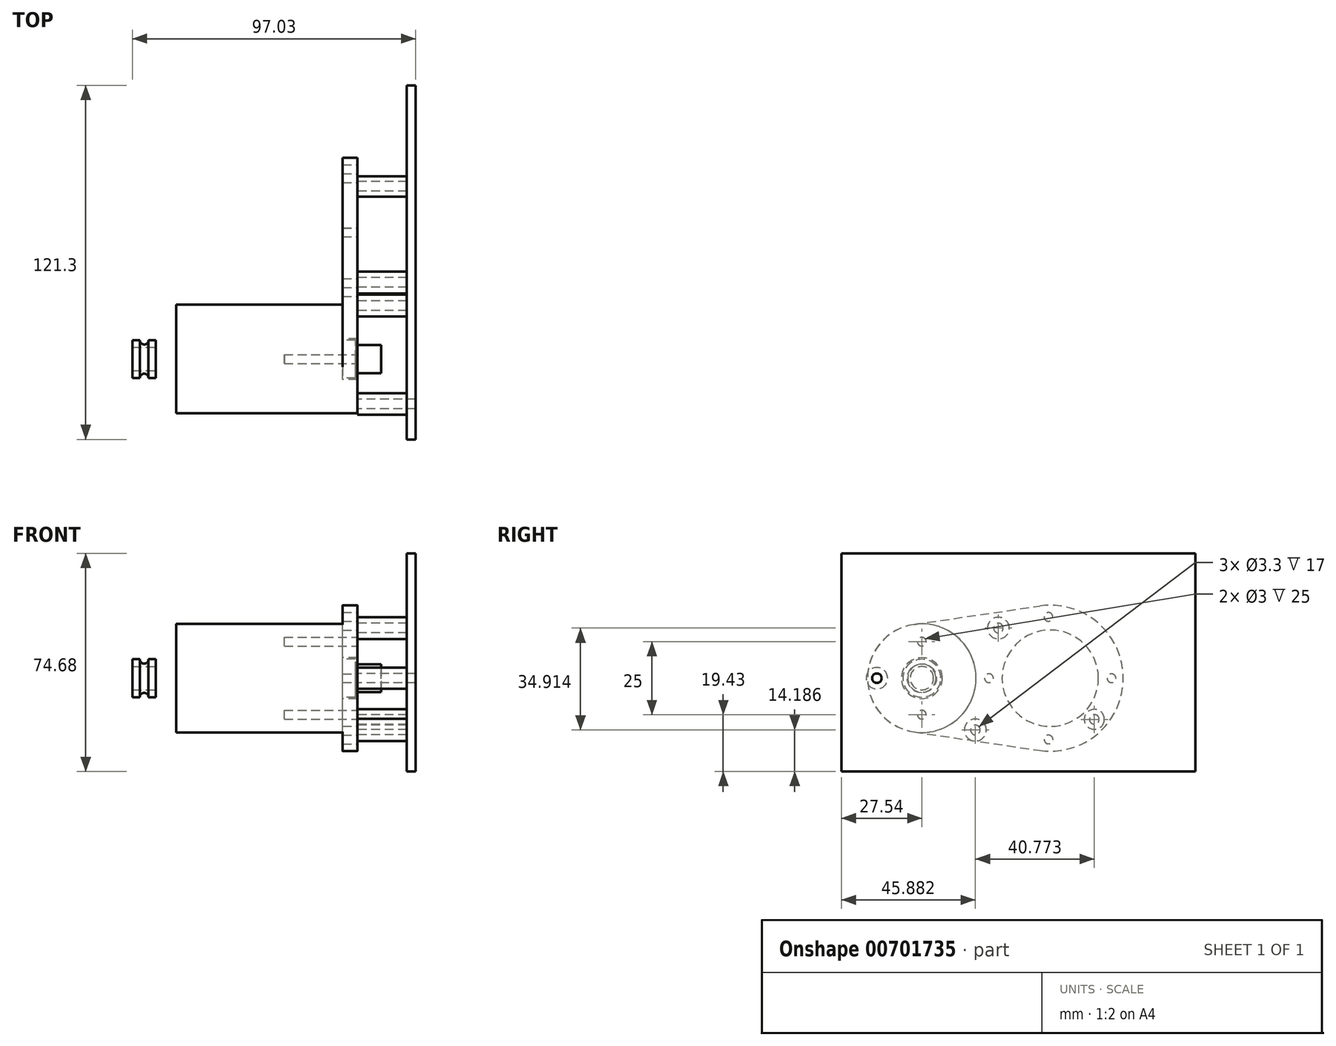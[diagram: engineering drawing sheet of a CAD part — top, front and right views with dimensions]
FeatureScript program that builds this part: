
annotation { "Feature Type Name" : "Feature", "Feature Type Description" : "" }
export const myFeature = defineFeature(function(context is Context, id is Id, definition is map)
    precondition{}
    {
        {
            var Q0;
            Q0=qCreatedBy(makeId("Right.planeOp"),FACE);
            var sketch = newSketch(context, id + "F0", { "sketchPlane" : qUnion([Q0])});
            skCircle(sketch, "E0", {"center": v(0, 0) * mm, "radius": 18.6 * mm});
            skSolve(sketch);
        }
        {
            var Q0;
            Q0=makeQuery(id+"F0.imprint","IMPRINT",FACE,{"disambiguationData":[TD([[makeQuery(id+"F0.imprint","IMPRINT",EDGE,{"derivedFrom":sQuery(id+"F0.wireOp",EDGE,"E0")}),1.0]])]});
            extrude(context, id + "F1", {"entities" : qUnion([Q0]), "depth" : 57 * mm, "offsetDistance" : 25 * mm});
        }
        {
            var Q0;
            Q0=makeQuery(id+"F1.opExtrude","CAP_FACE",FACE,{"disambiguationData":[OSD([sQuery(id+"F0.wireOp",EDGE,"E0")])],"isStart":false});
            var sketch = newSketch(context, id + "F2", { "sketchPlane" : qUnion([Q0])});
            skCircle(sketch, "E1", {"center": v(0, 0) * mm, "radius": 6.5 * mm});
            skSolve(sketch);
        }
        {
            var Q0;
            Q0=makeQuery(id+"F2.imprint","IMPRINT",FACE,{"disambiguationData":[TD([[makeQuery(id+"F2.imprint","IMPRINT",EDGE,{"derivedFrom":sQuery(id+"F2.wireOp",EDGE,"E1")}),1.0]])]});
            extrude(context, id + "F3", {"entities" : qUnion([Q0]), "operationType" : NewBodyOperationType.ADD, "depth" : 4.4 * mm, "offsetDistance" : 25 * mm});
        }
        {
            var Q0;
            Q0=makeQuery(id+"F3.opExtrude","CAP_FACE",FACE,{"disambiguationData":[OSD([sQuery(id+"F2.wireOp",EDGE,"E1")])],"isStart":false});
            var sketch = newSketch(context, id + "F4", { "sketchPlane" : qUnion([Q0])});
            skCircle(sketch, "E2", {"center": v(0, 0) * mm, "radius": 4.8 * mm});
            skSolve(sketch);
        }
        {
            var Q0;
            Q0=makeQuery(id+"F4.imprint","IMPRINT",FACE,{"disambiguationData":[TD([[makeQuery(id+"F4.imprint","IMPRINT",EDGE,{"derivedFrom":sQuery(id+"F4.wireOp",EDGE,"E2")}),1.0]])]});
            extrude(context, id + "F5", {"entities" : qUnion([Q0]), "operationType" : NewBodyOperationType.ADD, "depth" : 8.8 * mm, "offsetDistance" : 25 * mm});
        }
        {
            var Q0;
            Q0=makeQuery(id+"F1.opExtrude","CAP_FACE",FACE,{"disambiguationData":[OSD([sQuery(id+"F0.wireOp",EDGE,"E0")])],"isStart":false});
            var sketch = newSketch(context, id + "F6", { "sketchPlane" : qUnion([Q0])});
            skCircle(sketch, "E3", {"center": v(0, 0) * mm, "radius": 7 * mm});
            skCircle(sketch, "E4", {"center": v(0, 0) * mm, "radius": 20 * mm});
            skSolve(sketch);
        }
        {
            var Q0;
            Q0=makeQuery(id+"F6.imprint","IMPRINT",FACE,{"disambiguationData":[TD([[makeQuery(id+"F6.imprint","IMPRINT",EDGE,{"derivedFrom":sQuery(id+"F6.wireOp",EDGE,"E3")}),-1.0]])]});
            extrude(context, id + "F7", {"entities" : qUnion([Q0]), "depth" : 5 * mm, "offsetDistance" : 25 * mm});
        }
        {
            var Q0;
            Q0=makeQuery(id+"F7.opExtrude","CAP_FACE",FACE,{"disambiguationData":[OSD([sQuery(id+"F0.wireOp",EDGE,"E0"),sQuery(id+"F6.wireOp",EDGE,"E3")])],"isStart":false});
            var sketch = newSketch(context, id + "F8", { "sketchPlane" : qUnion([Q0])});
            skCircle(sketch, "E5", {"center": v(45, 0) * mm, "radius": 25 * mm});
            skCircle(sketch, "E6", {"center": v(45, 0) * mm, "radius": 16.5 * mm});
            skSolve(sketch);
        }
        {
            var Q0;
            Q0=makeQuery(id+"F8.imprint","IMPRINT",FACE,{"disambiguationData":[TD([[makeQuery(id+"F8.imprint","IMPRINT",EDGE,{"derivedFrom":sQuery(id+"F8.wireOp",EDGE,"E5")}),1.0]])]});
            extrude(context, id + "F9", {"entities" : qUnion([Q0]), "oppositeDirection" : true, "depth" : 5 * mm, "offsetDistance" : 25 * mm});
        }
        {
            var Q0;
            Q0=makeQuery(id+"F9.opExtrude","SWEPT_BODY",BODY,{"disambiguationData":[OSD([sQuery(id+"F8.wireOp",EDGE,"E5"),sQuery(id+"F8.wireOp",EDGE,"E6")])]});
            deleteBodies(context, id + "F10", {"entities" : qUnion([Q0])});
        }
        {
            var Q0;
            Q0=makeQuery(id+"F7.opExtrude","CAP_FACE",FACE,{"disambiguationData":[OSD([sQuery(id+"F0.wireOp",EDGE,"E0"),sQuery(id+"F6.wireOp",EDGE,"E3")])],"isStart":false});
            var sketch = newSketch(context, id + "F11", { "sketchPlane" : qUnion([Q0])});
            skLineSegment(sketch, "E7", {"start": v(-2.7, 18.4) * mm, "end": v(40.36, 24.73) * mm});
            skLineSegment(sketch, "E8", {"start": v(-2.7, -18.4) * mm, "end": v(40.36, -24.73) * mm});
            skArc(sketch, "E9", {"start": v(40.36, 24.73) * mm, "mid": v(69, 0) * mm, "end": v(40.36, -24.73) * mm});
            skCircle(sketch, "E10", {"center": v(44, 0) * mm, "radius": 16.5 * mm});
            skArc(sketch, "E11", {"start": v(-2.7, 18.4) * mm, "mid": v(18.6, 0) * mm, "end": v(-2.7, -18.4) * mm});
            skSolve(sketch);
        }
        {
            var Q0;
            Q0=makeQuery(id+"F11.imprint","IMPRINT",FACE,{"disambiguationData":[TD([[makeQuery(id+"F11.imprint","IMPRINT",EDGE,{"derivedFrom":sQuery(id+"F11.wireOp",EDGE,"E7")}),-1.0]])]});
            extrude(context, id + "F12", {"entities" : qUnion([Q0]), "operationType" : NewBodyOperationType.ADD, "oppositeDirection" : true, "depth" : 5 * mm, "offsetDistance" : 25 * mm});
        }
        {
            var Q0;
            Q0=makeQuery(id+"F12.boolean.opBoolean","MERGE",FACE,{"derivedFrom":[makeQuery(id+"F7.opExtrude","CAP_FACE",FACE,{"disambiguationData":[OSD([sQuery(id+"F0.wireOp",EDGE,"E0"),sQuery(id+"F6.wireOp",EDGE,"E3")])],"isStart":false}),makeQuery(id+"F12.opExtrude","CAP_FACE",FACE,{"disambiguationData":[OSD([sQuery(id+"F11.wireOp",EDGE,"E7"),sQuery(id+"F11.wireOp",EDGE,"E8"),sQuery(id+"F11.wireOp",EDGE,"E9"),sQuery(id+"F11.wireOp",EDGE,"E10"),sQuery(id+"F11.wireOp",EDGE,"E11")])],"isStart":true})]});
            var sketch = newSketch(context, id + "F13", { "sketchPlane" : qUnion([Q0])});
            skCircle(sketch, "E12", {"center": v(0, 12.5) * mm, "radius": 1.5 * mm});
            skCircle(sketch, "E13", {"center": v(0, -12.5) * mm, "radius": 1.5 * mm});
            skSolve(sketch);
        }
        {
            var Q0;
            Q0=makeQuery(id+"F13.imprint","IMPRINT",FACE,{"disambiguationData":[TD([[makeQuery(id+"F13.imprint","IMPRINT",EDGE,{"derivedFrom":sQuery(id+"F13.wireOp",EDGE,"E12")}),1.0]])]});
            var Q1;
            Q1=makeQuery(id+"F13.imprint","IMPRINT",FACE,{"disambiguationData":[TD([[makeQuery(id+"F13.imprint","IMPRINT",EDGE,{"derivedFrom":sQuery(id+"F13.wireOp",EDGE,"E13")}),1.0]])]});
            extrude(context, id + "F14", {"entities" : qUnion([Q0, Q1]), "operationType" : NewBodyOperationType.REMOVE, "oppositeDirection" : true, "depth" : 25 * mm, "offsetDistance" : 25 * mm});
        }
        {
            var Q0;
            Q0=makeQuery(id+"F12.boolean.opBoolean","MERGE",FACE,{"derivedFrom":[makeQuery(id+"F7.opExtrude","CAP_FACE",FACE,{"disambiguationData":[OSD([sQuery(id+"F0.wireOp",EDGE,"E0"),sQuery(id+"F6.wireOp",EDGE,"E3")])],"isStart":false}),makeQuery(id+"F12.opExtrude","CAP_FACE",FACE,{"disambiguationData":[OSD([sQuery(id+"F11.wireOp",EDGE,"E7"),sQuery(id+"F11.wireOp",EDGE,"E8"),sQuery(id+"F11.wireOp",EDGE,"E9"),sQuery(id+"F11.wireOp",EDGE,"E10"),sQuery(id+"F11.wireOp",EDGE,"E11")])],"isStart":true})]});
            var sketch = newSketch(context, id + "F15", { "sketchPlane" : qUnion([Q0])});
            skCircle(sketch, "E14", {"center": v(44, 0) * mm, "radius": 21 * mm, "construction": true});
            skCircle(sketch, "E15", {"center": v(43.39, 21) * mm, "radius": 1.5 * mm});
            skCircle(sketch, "E16", {"center": v(65, 0) * mm, "radius": 1.5 * mm});
            skPoint(sketch, "E16.centerSnap0", {"position": v(69, 0) * mm});
            skCircle(sketch, "E17", {"center": v(43.43, -21) * mm, "radius": 1.5 * mm});
            skCircle(sketch, "E18", {"center": v(23, 0) * mm, "radius": 1.5 * mm});
            skSolve(sketch);
        }
        {
            var Q0;
            Q0=makeQuery(id+"F15.imprint","IMPRINT",FACE,{"disambiguationData":[TD([[makeQuery(id+"F15.imprint","IMPRINT",EDGE,{"derivedFrom":sQuery(id+"F15.wireOp",EDGE,"E18")}),1.0]])]});
            var Q1;
            Q1=makeQuery(id+"F15.imprint","IMPRINT",FACE,{"disambiguationData":[TD([[makeQuery(id+"F15.imprint","IMPRINT",EDGE,{"derivedFrom":sQuery(id+"F15.wireOp",EDGE,"E15")}),1.0]])]});
            var Q2;
            Q2=makeQuery(id+"F15.imprint","IMPRINT",FACE,{"disambiguationData":[TD([[makeQuery(id+"F15.imprint","IMPRINT",EDGE,{"derivedFrom":sQuery(id+"F15.wireOp",EDGE,"E16")}),1.0]])]});
            var Q3;
            Q3=makeQuery(id+"F15.imprint","IMPRINT",FACE,{"disambiguationData":[TD([[makeQuery(id+"F15.imprint","IMPRINT",EDGE,{"derivedFrom":sQuery(id+"F15.wireOp",EDGE,"E17")}),1.0]])]});
            extrude(context, id + "F16", {"entities" : qUnion([Q0, Q1, Q2, Q3]), "operationType" : NewBodyOperationType.REMOVE, "oppositeDirection" : true, "depth" : 25 * mm, "offsetDistance" : 25 * mm});
        }
        {
            var Q0;
            Q0=qCreatedBy(makeId("Front.planeOp"),FACE);
            var sketch = newSketch(context, id + "F17", { "sketchPlane" : qUnion([Q0])});
            skLineSegment(sketch, "E19", {"start": v(0, 0) * mm, "end": v(-20.34, 0) * mm});
            skLineSegment(sketch, "E20", {"start": v(-15.03, 4) * mm, "end": v(-15.03, 6.5) * mm});
            skLineSegment(sketch, "E21", {"start": v(-15.03, 6.5) * mm, "end": v(-12.53, 6.5) * mm});
            skLineSegment(sketch, "E22", {"start": v(-7.03, 4) * mm, "end": v(-7.03, 6.5) * mm});
            skLineSegment(sketch, "E23", {"start": v(-7.03, 6.5) * mm, "end": v(-9.53, 6.5) * mm});
            skLineSegment(sketch, "E24", {"start": v(-15.03, 4) * mm, "end": v(-7.03, 4) * mm});
            skArc(sketch, "E25", {"start": v(-12.53, 6.5) * mm, "mid": v(-11.03, 5) * mm, "end": v(-9.53, 6.5) * mm});
            skSolve(sketch);
        }
        {
            var Q0;
            Q0=makeQuery(id+"F17.imprint","IMPRINT",FACE,{"disambiguationData":[TD([[makeQuery(id+"F17.imprint","IMPRINT",EDGE,{"derivedFrom":sQuery(id+"F17.wireOp",EDGE,"E20")}),-1.0]])]});
            var Q1;
            Q1=sQuery(id+"F17.wireOp",EDGE,"E19");
            revolve(context, id + "F18", {"entities" : qUnion([Q0]), "axis" : qUnion([Q1]), "revolveType" : RevolveType.FULL});
        }
        {
            var Q0;
            Q0=makeQuery(id+"F12.boolean.opBoolean","MERGE",FACE,{"derivedFrom":[makeQuery(id+"F7.opExtrude","CAP_FACE",FACE,{"disambiguationData":[OSD([sQuery(id+"F0.wireOp",EDGE,"E0"),sQuery(id+"F6.wireOp",EDGE,"E3")])],"isStart":false}),makeQuery(id+"F12.opExtrude","CAP_FACE",FACE,{"disambiguationData":[OSD([sQuery(id+"F11.wireOp",EDGE,"E7"),sQuery(id+"F11.wireOp",EDGE,"E8"),sQuery(id+"F11.wireOp",EDGE,"E9"),sQuery(id+"F11.wireOp",EDGE,"E10"),sQuery(id+"F11.wireOp",EDGE,"E11")])],"isStart":true})]});
            var sketch = newSketch(context, id + "F19", { "sketchPlane" : qUnion([Q0])});
            skCircle(sketch, "E26", {"center": v(0, 0) * mm, "radius": 7 * mm});
            skCircle(sketch, "E27", {"center": v(44, 0) * mm, "radius": 37 * mm});
            skSolve(sketch);
        }
        {
            var Q0;
            {var subQ1=sQuery(id+"F19.wireOp",EDGE,"E26");Q0=makeQuery(id+"F19.imprint","IMPRINT",FACE,{"disambiguationData":[TD([[makeQuery(id+"F19.imprint","IMPRINT",EDGE,{"derivedFrom":subQ1}),-1.0]])]});}
            var sketch = newSketch(context, id + "F20", { "sketchPlane" : qUnion([Q0])});
            skCircle(sketch, "E28", {"center": v(-15.42, 0) * mm, "radius": 1.65 * mm});
            skCircle(sketch, "E29", {"center": v(26.23, 17.17) * mm, "radius": 1.65 * mm});
            skCircle(sketch, "E30", {"center": v(59.11, -14.1) * mm, "radius": 1.65 * mm});
            skCircle(sketch, "E31", {"center": v(18.34, -17.74) * mm, "radius": 1.65 * mm});
            skCircle(sketch, "E32", {"center": v(26.23, 17.17) * mm, "radius": 3.73 * mm});
            skCircle(sketch, "E33", {"center": v(59.11, -14.1) * mm, "radius": 3.44 * mm});
            skCircle(sketch, "E34", {"center": v(18.34, -17.74) * mm, "radius": 3.78 * mm});
            skCircle(sketch, "E35", {"center": v(-15.42, 0) * mm, "radius": 3.68 * mm});
            skSolve(sketch);
        }
        {
            var Q0;
            Q0=qSketchRegion(id+"F20",true);
            extrude(context, id + "F21", {"entities" : qUnion([Q0]), "depth" : 20 * mm, "offsetDistance" : 25 * mm});
        }
        {
            var Q0;
            Q0=makeQuery(id+"F21.opExtrude","CAP_FACE",FACE,{"disambiguationData":[OSD([sQuery(id+"F20.wireOp",EDGE,"E28"),sQuery(id+"F20.wireOp",EDGE,"E35")])],"isStart":false});
            var sketch = newSketch(context, id + "F22", { "sketchPlane" : qUnion([Q0])});
            skLineSegment(sketch, "E36.bottom", {"start": v(-27.54, 42.75) * mm, "end": v(93.76, 42.75) * mm});
            skLineSegment(sketch, "E36.top", {"start": v(-27.54, -31.93) * mm, "end": v(93.76, -31.93) * mm});
            skLineSegment(sketch, "E36.left", {"start": v(-27.54, 42.75) * mm, "end": v(-27.54, -31.93) * mm});
            skLineSegment(sketch, "E36.right", {"start": v(93.76, 42.75) * mm, "end": v(93.76, -31.93) * mm});
            skSolve(sketch);
        }
        {
            var Q0;
            Q0=makeQuery(id+"F22.imprint","IMPRINT",FACE,{"disambiguationData":[TD([[makeQuery(id+"F22.imprint","IMPRINT",EDGE,{"derivedFrom":sQuery(id+"F22.wireOp",EDGE,"E36.bottom")}),-1.0]])]});
            extrude(context, id + "F23", {"entities" : qUnion([Q0]), "operationType" : NewBodyOperationType.ADD, "oppositeDirection" : true, "depth" : 3 * mm, "offsetDistance" : 25 * mm});
        }
    });
